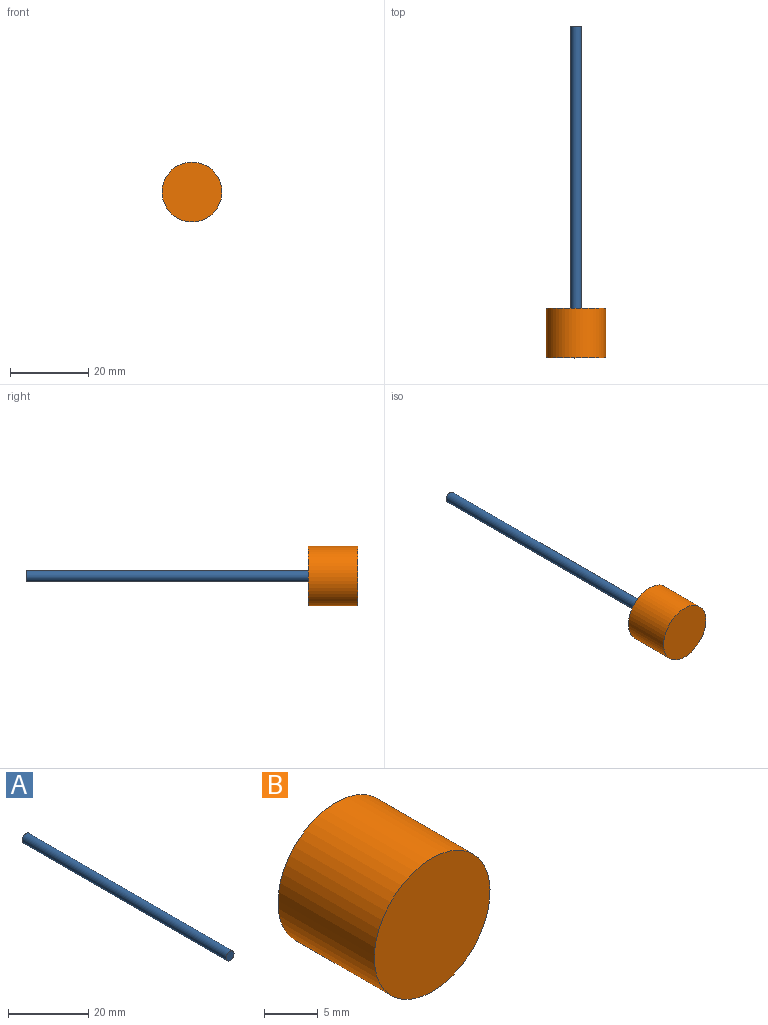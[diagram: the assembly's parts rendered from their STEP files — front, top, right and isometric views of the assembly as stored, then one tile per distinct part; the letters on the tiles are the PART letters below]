
ASSEMBLY  parts=2 mates=1
PART A: 3 faces, bbox 2.8x71.9x2.8 mm
  f0: cylinder r=1.4mm len=71.88mm, axis (0,1,0), area 631mm2, adj f1,f2
  f1: plane 2.79x2.79mm, normal (0,-1,0), area 6.1mm2, adj f0
  f2: plane 2.79x2.79mm, normal (0,1,0), area 6.1mm2, adj f0
PART B: 3 faces, bbox 15.2x12.7x15.2 mm
  f0: cylinder r=7.62mm len=15.24mm, axis (0,1,0), area 608mm2, adj f1,f2
  f1: plane 15.24x15.24mm, normal (0,-1,0), area 182.4mm2, adj f0
  f2: plane 15.24x15.24mm, normal (0,1,0), area 182.4mm2, adj f0
PLACE A rot(axis=(0.07,0.99,0.16),0deg) t=(22.78,30.89,-9.66)mm
PLACE B rot(axis=(-1,0,0),180deg) t=(22.78,-53.69,-9.66)mm
MATE revolute B.f0 <-> A.f0  axis (0,1,0) through (22.78,-40.99,-9.66)mm
